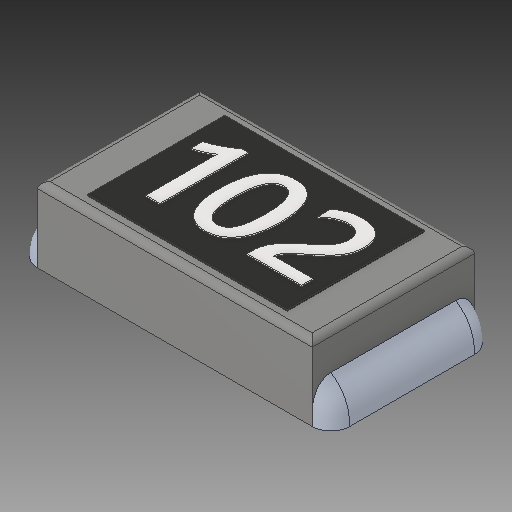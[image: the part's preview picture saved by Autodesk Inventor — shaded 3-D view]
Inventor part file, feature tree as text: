
AUTODESK INVENTOR PART (.ipt)
format: ipt  version: 2018.3 (Build 223284000, 284)  size: 250,368 bytes
history: native  units: mm
features: other x4, fillet x1, mirror x1
ambient origin geometry x8: Origin, YZ Plane, XZ Plane, XY Plane, X Axis, Y Axis, Z Axis, Center Point
bodies: Body1 (feature_tree), Body2 (feature_tree), Body3 (feature_tree)
feature tree (6):
  other  "Sólido1"
  other  "Sólido2"
  other  "Sólido3"
  fillet  "Fillet2"  [1 undecoded]
  mirror  "Mirror1"
  other  "Boss-Extrude4"
note: 1 required parameter value undecoded (feature->parameter linkage not recoverable at this tier; creation-order binding heuristic only, values carry confidence <= 0.55)
